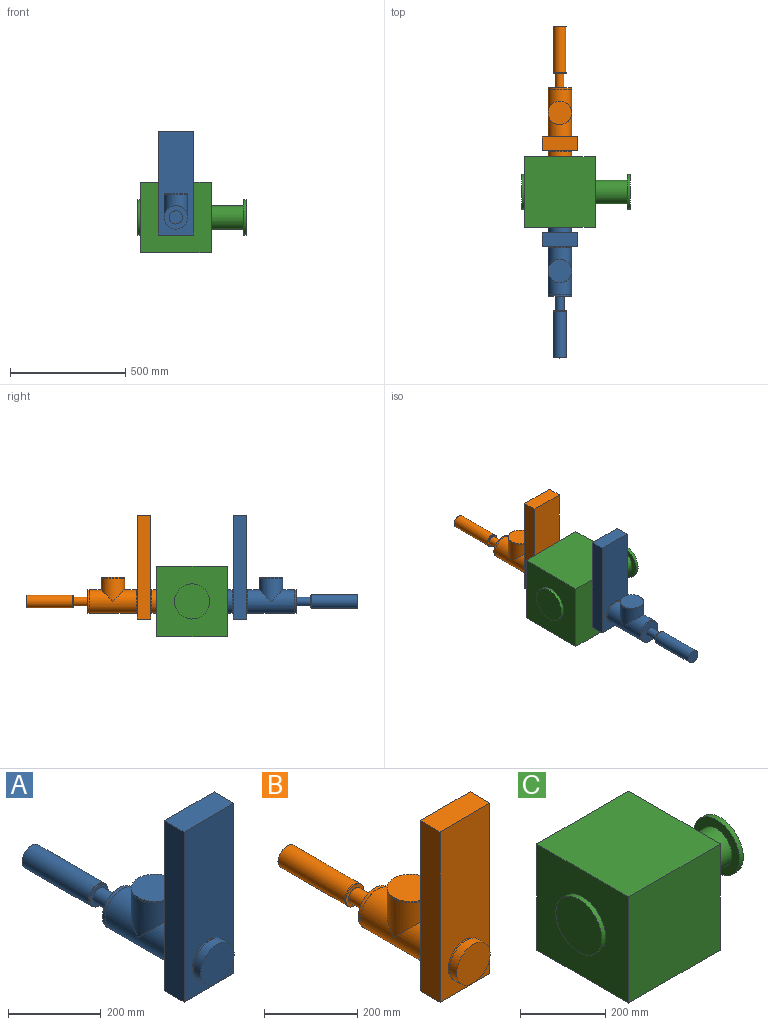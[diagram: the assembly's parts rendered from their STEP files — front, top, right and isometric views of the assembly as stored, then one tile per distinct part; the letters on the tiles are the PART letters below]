
ASSEMBLY  parts=3 mates=2
PART A: 26 faces, bbox 151.9x566.6x448.8 mm
  f0: cylinder r=50.8mm len=202.18mm, axis (0,-1,0), area 54211.7mm2, adj f12,f14,f15
  f1: cylinder r=50.8mm len=101.6mm, axis (0,-1,0), area 6891.2mm2, adj f2,f4
  f2: plane 101.6x101.6mm, normal (0,-1,0), area 8107.3mm2, adj f1
  f3: cylinder r=51mm len=102.01mm, axis (0,-1,0), area 1221mm2, adj f4,f10
  f4: plane 102.01x102.01mm, normal (0,-1,0), area 65mm2, adj f1,f3
  f5: plane 448.82x59.94mm, normal (1,0,0), area 26903.9mm2, adj f6,f8,f9,f10
  f6: plane 151.89x59.94mm, normal (0,0,-1), area 9105mm2, adj f5,f7,f9,f10
  f7: plane 448.82x59.94mm, normal (-1,0,0), area 26903.9mm2, adj f6,f8,f9,f10
  f8: plane 151.89x59.94mm, normal (0,0,1), area 9105mm2, adj f5,f7,f9,f10
  f9: plane 448.82x151.89mm, normal (0,1,0), area 59999.6mm2, adj f5,f6,f7,f8,f11
  f10: plane 448.82x151.89mm, normal (0,-1,0), area 59999.6mm2, adj f3,f5,f6,f7,f8
  f11: cylinder r=51mm len=102.01mm, axis (0,-1,0), area 1221mm2, adj f9,f12
  f12: plane 102.01x102.01mm, normal (0,1,0), area 65mm2, adj f0,f11
  f13: cylinder r=51mm len=102.01mm, axis (0,-1,0), area 2441.9mm2, adj f14,f19
  f14: plane 102.01x102.01mm, normal (0,-1,0), area 65mm2, adj f0,f13
  f15: cylinder r=50.8mm len=101.6mm, axis (0,0,-1), area 21944.6mm2, adj f0,f18
  f16: cylinder r=51mm len=102.01mm, axis (0,0,-1), area 1221mm2, adj f17,f18
  f17: plane 102.01x102.01mm, normal (0,0,1), area 8172.3mm2, adj f16
  f18: plane 102.01x102.01mm, normal (0,0,-1), area 65mm2, adj f15,f16
  f19: plane 102.01x102.01mm, normal (0,1,0), area 7032.2mm2, adj f13,f20
  f20: cylinder r=19.05mm len=61.4mm, axis (0,-1,0), area 7349.8mm2, adj f19,f22
  f21: cylinder r=27.43mm len=54.86mm, axis (0,-1,0), area 525.4mm2, adj f22,f25
  f22: plane 54.86x54.86mm, normal (0,-1,0), area 1224mm2, adj f20,f21
  f23: cylinder r=28.57mm len=203.2mm, axis (0,-1,0), area 36480.9mm2, adj f24,f25
  f24: plane 57.15x57.15mm, normal (0,1,0), area 2564.9mm2, adj f23
  f25: plane 57.15x57.15mm, normal (0,-1,0), area 200.8mm2, adj f21,f23
PART B: 26 faces, bbox 151.9x566.6x448.8 mm
  f0: cylinder r=50.8mm len=202.18mm, axis (0,-1,0), area 54211.7mm2, adj f12,f14,f15
  f1: cylinder r=50.8mm len=101.6mm, axis (0,-1,0), area 6891.2mm2, adj f2,f4
  f2: plane 101.6x101.6mm, normal (0,-1,0), area 8107.3mm2, adj f1
  f3: cylinder r=51mm len=102.01mm, axis (0,-1,0), area 1221mm2, adj f4,f10
  f4: plane 102.01x102.01mm, normal (0,-1,0), area 65mm2, adj f1,f3
  f5: plane 448.82x59.94mm, normal (1,0,0), area 26903.9mm2, adj f6,f8,f9,f10
  f6: plane 151.89x59.94mm, normal (0,0,-1), area 9105mm2, adj f5,f7,f9,f10
  f7: plane 448.82x59.94mm, normal (-1,0,0), area 26903.9mm2, adj f6,f8,f9,f10
  f8: plane 151.89x59.94mm, normal (0,0,1), area 9105mm2, adj f5,f7,f9,f10
  f9: plane 448.82x151.89mm, normal (0,1,0), area 59999.6mm2, adj f5,f6,f7,f8,f11
  f10: plane 448.82x151.89mm, normal (0,-1,0), area 59999.6mm2, adj f3,f5,f6,f7,f8
  f11: cylinder r=51mm len=102.01mm, axis (0,-1,0), area 1221mm2, adj f9,f12
  f12: plane 102.01x102.01mm, normal (0,1,0), area 65mm2, adj f0,f11
  f13: cylinder r=51mm len=102.01mm, axis (0,-1,0), area 2441.9mm2, adj f14,f19
  f14: plane 102.01x102.01mm, normal (0,-1,0), area 65mm2, adj f0,f13
  f15: cylinder r=50.8mm len=101.6mm, axis (0,0,-1), area 21944.6mm2, adj f0,f18
  f16: cylinder r=51mm len=102.01mm, axis (0,0,-1), area 1221mm2, adj f17,f18
  f17: plane 102.01x102.01mm, normal (0,0,1), area 8172.3mm2, adj f16
  f18: plane 102.01x102.01mm, normal (0,0,-1), area 65mm2, adj f15,f16
  f19: plane 102.01x102.01mm, normal (0,1,0), area 7032.2mm2, adj f13,f20
  f20: cylinder r=19.05mm len=61.4mm, axis (0,-1,0), area 7349.8mm2, adj f19,f23
  f21: cylinder r=27.43mm len=54.86mm, axis (0,-1,0), area 525.4mm2, adj f22,f23
  f22: plane 54.86x54.86mm, normal (0,1,0), area 8.9mm2, adj f21,f24
  f23: plane 54.86x54.86mm, normal (0,-1,0), area 1224mm2, adj f20,f21
  f24: cylinder r=27.38mm len=203.2mm, axis (0,-1,0), area 34957.3mm2, adj f22,f25
  f25: plane 54.76x54.76mm, normal (0,1,0), area 2355.2mm2, adj f24
PART C: 14 faces, bbox 469.9x304.8x304.8 mm
  f0: plane 304.8x304.8mm, normal (0,1,0), area 92903mm2, adj f1,f3,f4,f5
  f1: plane 304.8x304.8mm, normal (-1,0,0), area 84795.7mm2, adj f0,f2,f4,f5,f10
  f2: plane 304.8x304.8mm, normal (0,-1,0), area 92903mm2, adj f1,f3,f4,f5
  f3: plane 304.8x304.8mm, normal (1,0,0), area 84795.7mm2, adj f0,f2,f4,f5,f6
  f4: plane 304.8x304.8mm, normal (0,0,1), area 92903mm2, adj f0,f1,f2,f3
  f5: plane 304.8x304.8mm, normal (0,0,-1), area 92903mm2, adj f0,f1,f2,f3
  f6: cylinder r=50.8mm len=139.7mm, axis (-1,0,0), area 44590.3mm2, adj f3,f9
  f7: cylinder r=76.2mm len=152.4mm, axis (-1,0,0), area 6080.5mm2, adj f8,f9
  f8: plane 152.4x152.4mm, normal (1,0,0), area 18241.5mm2, adj f7
  f9: plane 152.4x152.4mm, normal (-1,0,0), area 10134.1mm2, adj f6,f7
  f10: cylinder r=50.8mm len=101.6mm, axis (1,0,0), area 8.1mm2, adj f1,f13
  f11: cylinder r=76.2mm len=152.4mm, axis (1,0,0), area 6080.5mm2, adj f12,f13
  f12: plane 152.4x152.4mm, normal (-1,0,0), area 18241.5mm2, adj f11
  f13: plane 152.4x152.4mm, normal (1,0,0), area 10134.1mm2, adj f10,f11
PLACE A rot(axis=(0,0,1),180deg) t=(51.3,-835.07,24.72)mm
PLACE B t=(34.06,-148.58,24.72)mm
PLACE C rot(axis=(0,0,1),0deg) t=(34.06,-21.58,24.72)mm
MATE planar C.f2 <-> A.f0  axis (0,-1,0) through (42.68,-136.23,177.12)mm
MATE planar B.f0 <-> C.f0  axis (0,-1,0) through (42.68,168.57,177.12)mm
